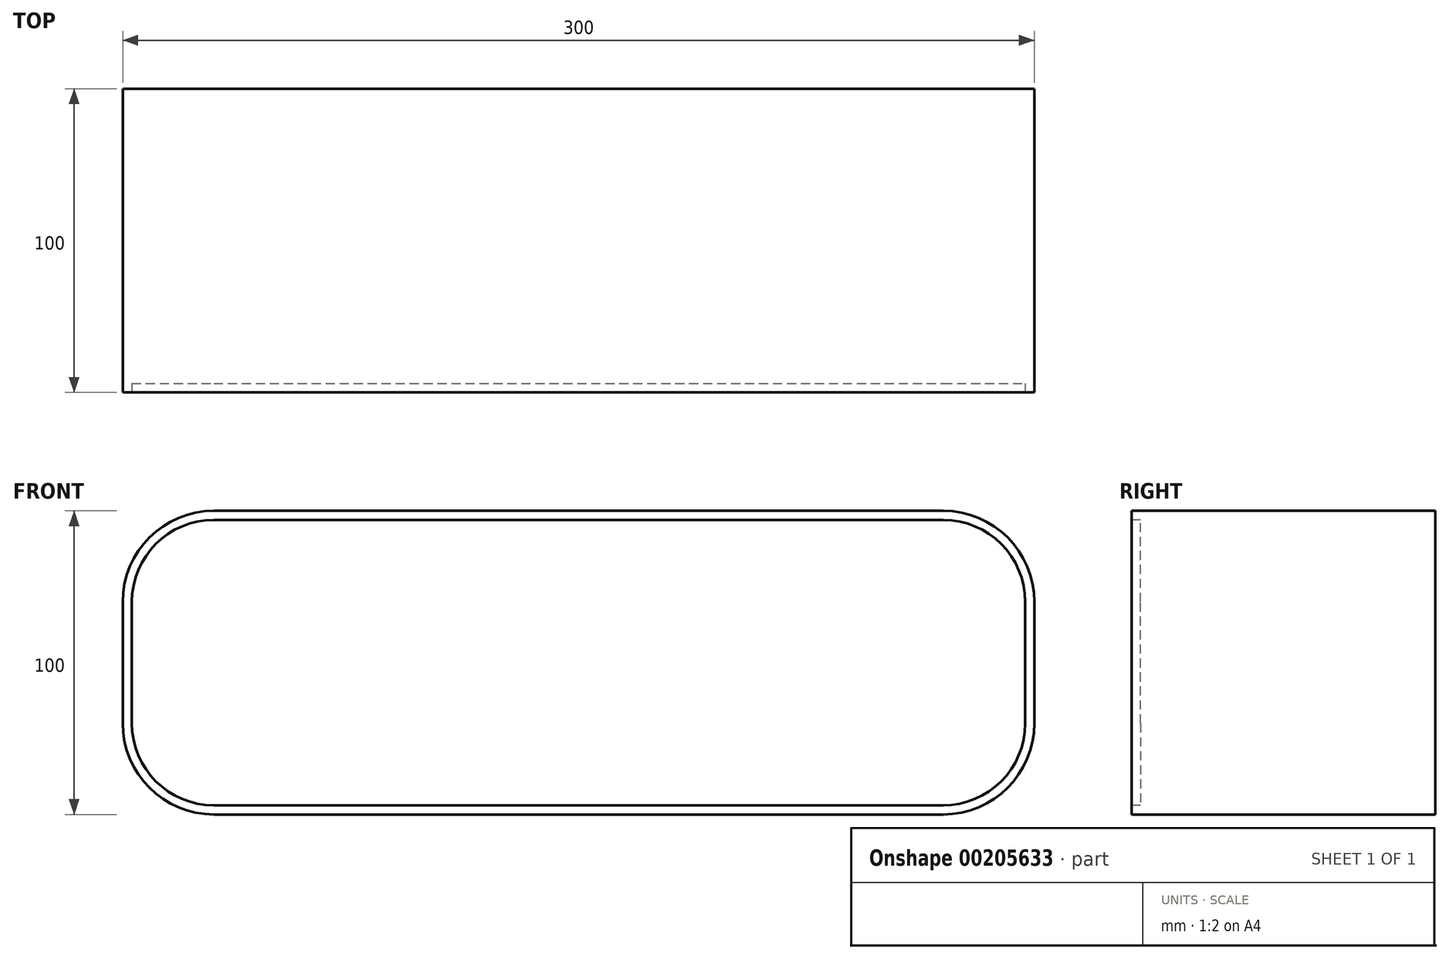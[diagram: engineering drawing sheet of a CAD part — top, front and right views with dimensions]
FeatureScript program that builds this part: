
annotation { "Feature Type Name" : "Feature", "Feature Type Description" : "" }
export const myFeature = defineFeature(function(context is Context, id is Id, definition is map)
    precondition{}
    {
        {
            var Q0;
            Q0=qCreatedBy(makeId("Front.planeOp"),FACE);
            var sketch = newSketch(context, id + "F0", { "sketchPlane" : qUnion([Q0])});
            skLineSegment(sketch, "E0.bottom", {"start": v(0, 0) * mm, "end": v(300, 0) * mm});
            skLineSegment(sketch, "E0.top", {"start": v(0, 100) * mm, "end": v(300, 100) * mm});
            skLineSegment(sketch, "E0.left", {"start": v(0, 0) * mm, "end": v(0, 100) * mm});
            skLineSegment(sketch, "E0.right", {"start": v(300, 0) * mm, "end": v(300, 100) * mm});
            skSolve(sketch);
        }
        {
            var Q0;
            Q0=makeQuery(id+"F0.imprint","IMPRINT",FACE,{"disambiguationData":[TD([[makeQuery(id+"F0.imprint","IMPRINT",EDGE,{"derivedFrom":sQuery(id+"F0.wireOp",EDGE,"E0.bottom")}),1.0]])]});
            extrude(context, id + "F1", {"entities" : qUnion([Q0]), "endBound" : BoundingType.SYMMETRIC, "oppositeDirection" : true, "depth" : 100 * mm});
        }
        {
            var Q0;
            Q0=makeQuery(id+"F1.opExtrude","SWEPT_EDGE",EDGE,{"disambiguationData":[OSD([sQuery(id+"F0.wireOp",EDGE,"E0.top"),sQuery(id+"F0.wireOp",EDGE,"E0.left")])]});
            var Q1;
            Q1=makeQuery(id+"F1.opExtrude","SWEPT_EDGE",EDGE,{"disambiguationData":[OSD([sQuery(id+"F0.wireOp",EDGE,"E0.bottom"),sQuery(id+"F0.wireOp",EDGE,"E0.left")])]});
            var Q2;
            Q2=makeQuery(id+"F1.opExtrude","SWEPT_EDGE",EDGE,{"disambiguationData":[OSD([sQuery(id+"F0.wireOp",EDGE,"E0.top"),sQuery(id+"F0.wireOp",EDGE,"E0.right")])]});
            var Q3;
            Q3=makeQuery(id+"F1.opExtrude","SWEPT_EDGE",EDGE,{"disambiguationData":[OSD([sQuery(id+"F0.wireOp",EDGE,"E0.bottom"),sQuery(id+"F0.wireOp",EDGE,"E0.right")])]});
            fillet(context, id + "F2", {"entities" : qUnion([Q0, Q1, Q2, Q3]), "radius" : 30 * mm, "tangentPropagation" : true, "allowEdgeOverflow" : false});
        }
        {
            var Q0;
            Q0=makeQuery(id+"F1.opExtrude","CAP_FACE",FACE,{"disambiguationData":[OSD([sQuery(id+"F0.wireOp",EDGE,"E0.bottom"),sQuery(id+"F0.wireOp",EDGE,"E0.top"),sQuery(id+"F0.wireOp",EDGE,"E0.left"),sQuery(id+"F0.wireOp",EDGE,"E0.right")])],"isStart":true});
            var sketch = newSketch(context, id + "F4", { "sketchPlane" : qUnion([Q0])});
            skLineSegment(sketch, "E1.0", {"start": v(30, 100) * mm, "end": v(270, 100) * mm, "construction": true});
            skArc(sketch, "E2.0", {"start": v(30, 100) * mm, "mid": v(8.79, 91.21) * mm, "end": v(0, 70) * mm, "construction": true});
            skLineSegment(sketch, "E3.0", {"start": v(0, 30) * mm, "end": v(0, 70) * mm, "construction": true});
            skArc(sketch, "E4.0", {"start": v(0, 30) * mm, "mid": v(8.79, 8.79) * mm, "end": v(30, 0) * mm, "construction": true});
            skLineSegment(sketch, "E5.0", {"start": v(30, 0) * mm, "end": v(270, 0) * mm, "construction": true});
            skArc(sketch, "E6.0", {"start": v(300, 70) * mm, "mid": v(291.21, 91.21) * mm, "end": v(270, 100) * mm, "construction": true});
            skLineSegment(sketch, "E7.0", {"start": v(300, 30) * mm, "end": v(300, 70) * mm, "construction": true});
            skArc(sketch, "E8.0", {"start": v(270, 0) * mm, "mid": v(291.21, 8.79) * mm, "end": v(300, 30) * mm, "construction": true});
            skLineSegment(sketch, "E9.0", {"start": v(30, 3) * mm, "end": v(270, 3) * mm});
            skArc(sketch, "E9.1", {"start": v(3, 30) * mm, "mid": v(10.9, 10.9) * mm, "end": v(30, 3) * mm});
            skArc(sketch, "E9.2", {"start": v(270, 3) * mm, "mid": v(289.1, 10.9) * mm, "end": v(297, 30) * mm});
            skLineSegment(sketch, "E9.3", {"start": v(3, 30) * mm, "end": v(3, 70) * mm});
            skLineSegment(sketch, "E9.4", {"start": v(297, 30) * mm, "end": v(297, 70) * mm});
            skArc(sketch, "E9.5", {"start": v(297, 70) * mm, "mid": v(289.1, 89.1) * mm, "end": v(270, 97) * mm});
            skLineSegment(sketch, "E9.6", {"start": v(30, 97) * mm, "end": v(270, 97) * mm});
            skArc(sketch, "E9.7", {"start": v(30, 97) * mm, "mid": v(10.9, 89.1) * mm, "end": v(3, 70) * mm});
            skSolve(sketch);
        }
        {
            var Q0;
            Q0=makeQuery(id+"F4.imprint","IMPRINT",FACE,{"disambiguationData":[TD([[makeQuery(id+"F4.imprint","IMPRINT",EDGE,{"derivedFrom":sQuery(id+"F4.wireOp",EDGE,"E9.0")}),1.0]])]});
            extrude(context, id + "F3", {"entities" : qUnion([Q0]), "operationType" : NewBodyOperationType.REMOVE, "oppositeDirection" : true, "depth" : 3 * mm});
        }
    });
